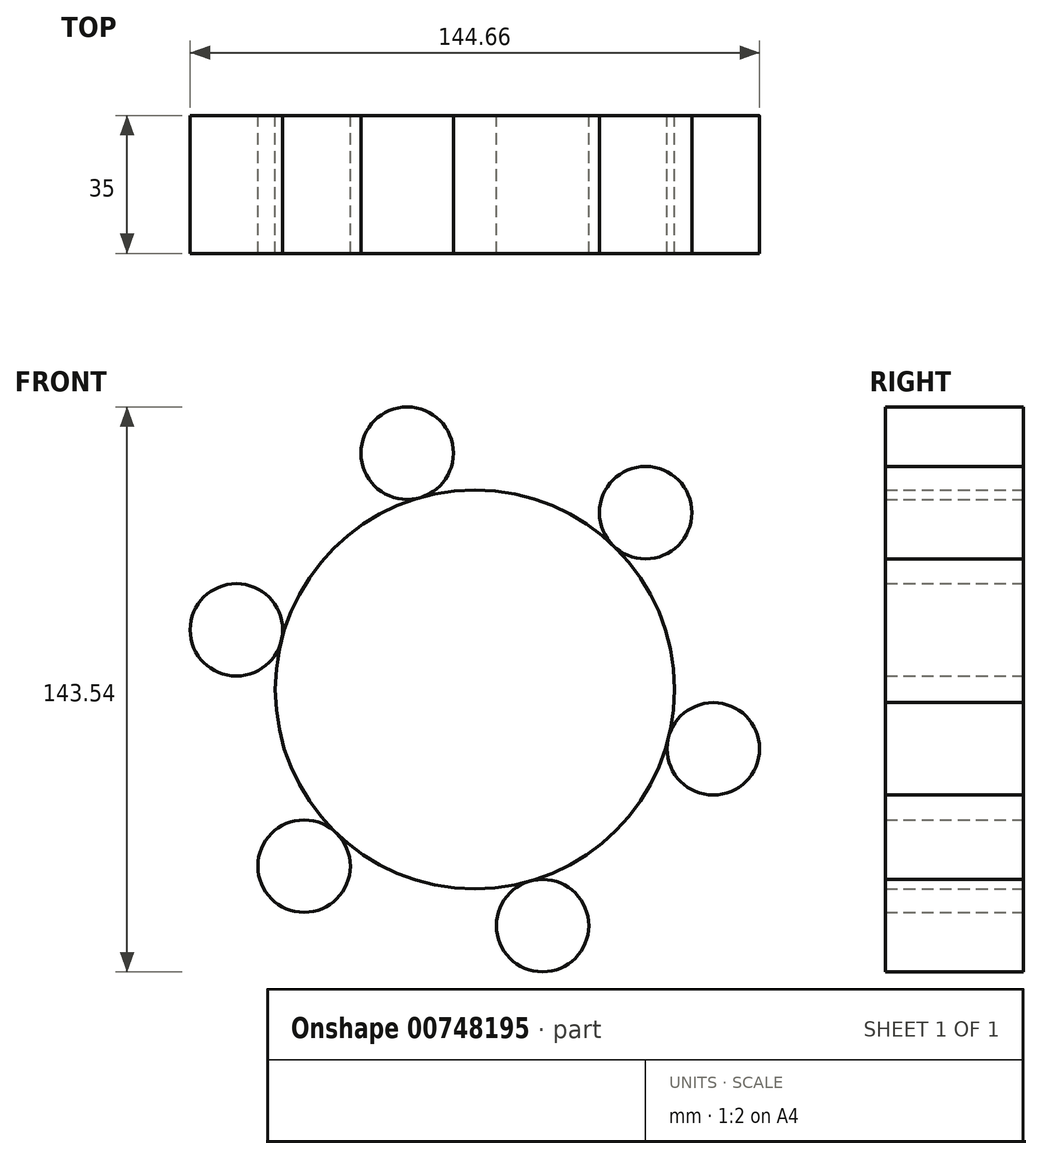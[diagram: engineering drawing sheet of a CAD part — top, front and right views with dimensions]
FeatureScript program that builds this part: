
annotation { "Feature Type Name" : "Feature", "Feature Type Description" : "" }
export const myFeature = defineFeature(function(context is Context, id is Id, definition is map)
    precondition{}
    {
        {
            var Q0;
            Q0=qCreatedBy(makeId("Front.planeOp"),FACE);
            var sketch = newSketch(context, id + "F0", { "sketchPlane" : qUnion([Q0])});
            skCircle(sketch, "E0", {"center": v(0, 0) * mm, "radius": 50.7 * mm});
            skCircle(sketch, "E1", {"center": v(-43.38, -44.91) * mm, "radius": 11.74 * mm});
            skSolve(sketch);
        }
        {
            var Q0;
            {var subQ0=sQuery(id+"F0.wireOp",EDGE,"E0");Q0=makeQuery(id+"F0.imprint","IMPRINT",FACE,{"disambiguationData":[TD([[makeQuery(id+"F0.imprint","IMPRINT",EDGE,{"disambiguationData":[TD([[makeQuery(id+"F0.imprint","INTERSECT",VERTEX,{"derivedFrom":[subQ0,sQuery(id+"F0.wireOp",EDGE,"E1")]}),-1.0]])],"derivedFrom":subQ0}),1.0]])]});}
            var Q1;
            {var subQ0=sQuery(id+"F0.wireOp",EDGE,"E1");Q1=makeQuery(id+"F0.imprint","IMPRINT",FACE,{"disambiguationData":[TD([[makeQuery(id+"F0.imprint","IMPRINT",EDGE,{"disambiguationData":[TD([[makeQuery(id+"F0.imprint","INTERSECT",VERTEX,{"derivedFrom":[sQuery(id+"F0.wireOp",EDGE,"E0"),subQ0]}),-1.0]])],"derivedFrom":subQ0}),1.0]])]});}
            extrude(context, id + "F1", {"entities" : qUnion([Q0, Q1]), "depth" : 35 * mm, "offsetDistance" : 25 * mm});
        }
        {
            var Q0;
            Q0=makeQuery(id+"F1.opExtrude","SWEPT_BODY",BODY,{"disambiguationData":[OSD([sQuery(id+"F0.wireOp",EDGE,"E1")])]});
            var Q1;
            Q1=makeQuery(id+"F1.opExtrude","CAP_EDGE",EDGE,{"disambiguationData":[OSD([sQuery(id+"F0.wireOp",EDGE,"E0")])],"isStart":false});
            circularPattern(context, id + "F2", {"entities" : qUnion([Q0]), "axis" : qUnion([Q1]), "angle" : 360 * degree, "instanceCount" : 6, "equalSpace" : true});
        }
    });
